# Revit family: Lighting-Industrial-GEWISS-ELIA-WL-LED_WATERTIGHT
name_source: partatom
category: Apparecchi per illuminazione
units: mm (PartAtom-declared; Revit-internal decimal feet)

## family parameters
Condiviso = No
Host = Superficie
Punto di calcolo locali = Sì
Quota connettore circolare = Usa diametro
Sorgente d'illuminazione = Sì
Taglio con vuoti quando caricato = No
Tipo di parte = Normale

## types (6) — shared parameters
Angolo inclinazione = 90.00°
Application = Indoor
Catalogue = LIGHTING
Catalogue Range = ELIA WL
Colour = White
Colour temperature = 4000K
Colour temperature: = 4000K
Emetti da lunghezza linea = 610 mm
File diagramma fotometrico = GWS2358PL.IES
Filtro dei colori = 16777215
IDF = 676f49d4-4ff3-43c5-861b-19ef4ef8a3b1
IDT = 94634168-d726-4c19-9922-7cff39855ded
Immagine tipo = ELIA_WL.jpeg
Installation = Ceiling - Wall mounted - Suspended
Insulation class = I
LED Life time (L80B50) = L80 B50 (Tq25°) = 54.000h
L_lampada = 1500 mm  [stored 4.92126 ft]
Lamp = LED
Optic = Opal
Produttore = GEWISS S.p.A.
Prospetto di default = 1219 mm
SEO = Ceiling - Wall mounted - Suspended
Shock resistance = IK08
Technical sheet = https://www.gewiss.com
Type of lamp = LED
Type of light source = LED - Not replaceable
Typology = Ceiling - Wall mounted - Suspended
URL = https://www.gewiss.com
Variazione temperatura colore lampada con luminosità attenuata = <Nessuno>
Version file RFA = 20.0
Visibilità bidimensionale = 2D frontali : Elia WL 1500
Visibilità frontale = Frontale : 1500
Voltage = 220-240 VÂ
Warranty = 5 years

## per-type parameters (varying)
| type | Descrizione | Dimensions (mm) | IP degree | Lumen output (lm) | Modello | Operating temperature: | System power | Weight (kg) | Weight (kg): | Working temperature |
| GWS2336PE - ELIA WL 1200 OPAL 4000K EMERGENCY | ELIA WL 1200 OPAL 4000K EMERGENCY | 1200 mm | IP54 | 4500 | GWS2336PE | 0 +25 °C | 42W | 2,7 | 2,7 | 0 +25 °C |
| GWS2358PL - ELIA WL 1500 OPAL 4000K THROUGH LINE | ELIA WL 1500 OPAL 4000K THROUGH LINE | 1500 mm | IP66 | 5700 | GWS2358PL | -25 +40 °C | 47W | 2 | 2 | -25 +40 °C |
| GWS2358PE - ELIA WL 1500 OPAL 4000K EMERGENCY | ELIA WL 1500 OPAL 4000K EMERGENCY | 1500 mm | IP54 | 5700 | GWS2358PE | 0 +25 °C | 52W | 3 | 3 | 0 +25 °C |
| GWS2358P - ELIA WL 1500 OPAL 4000K STAND ALONE | ELIA WL 1500 OPAL 4000K STAND ALONE | 1500 mm | IP66 | 5700 | GWS2358P | -25 +40 °C | 47W | 2 | 2 | -25 +40 °C |
| GWS2336PL - ELIA WL 1200 OPAL 4000K THROUGH LINE | ELIA WL 1200 OPAL 4000K THROUGH LINE | 1200 mm | IP66 | 4500 | GWS2336PL | -25 +40 °C | 37W | 1,7 | 1,7 | -25 +40 °C |
| GWS2336P - ELIA WL 1200 OPAL 4000K STAND ALONE | ELIA WL 1200 OPAL 4000K STAND ALONE | 1200 mm | IP66 | 4500 | GWS2336P | -25 +40 °C | 37W | 1,7 | 1,7 | -25 +40 °C |

note: [stored X ft] marks values corroborated as IEEE doubles in the binary element streams (Revit-internal decimal feet)
